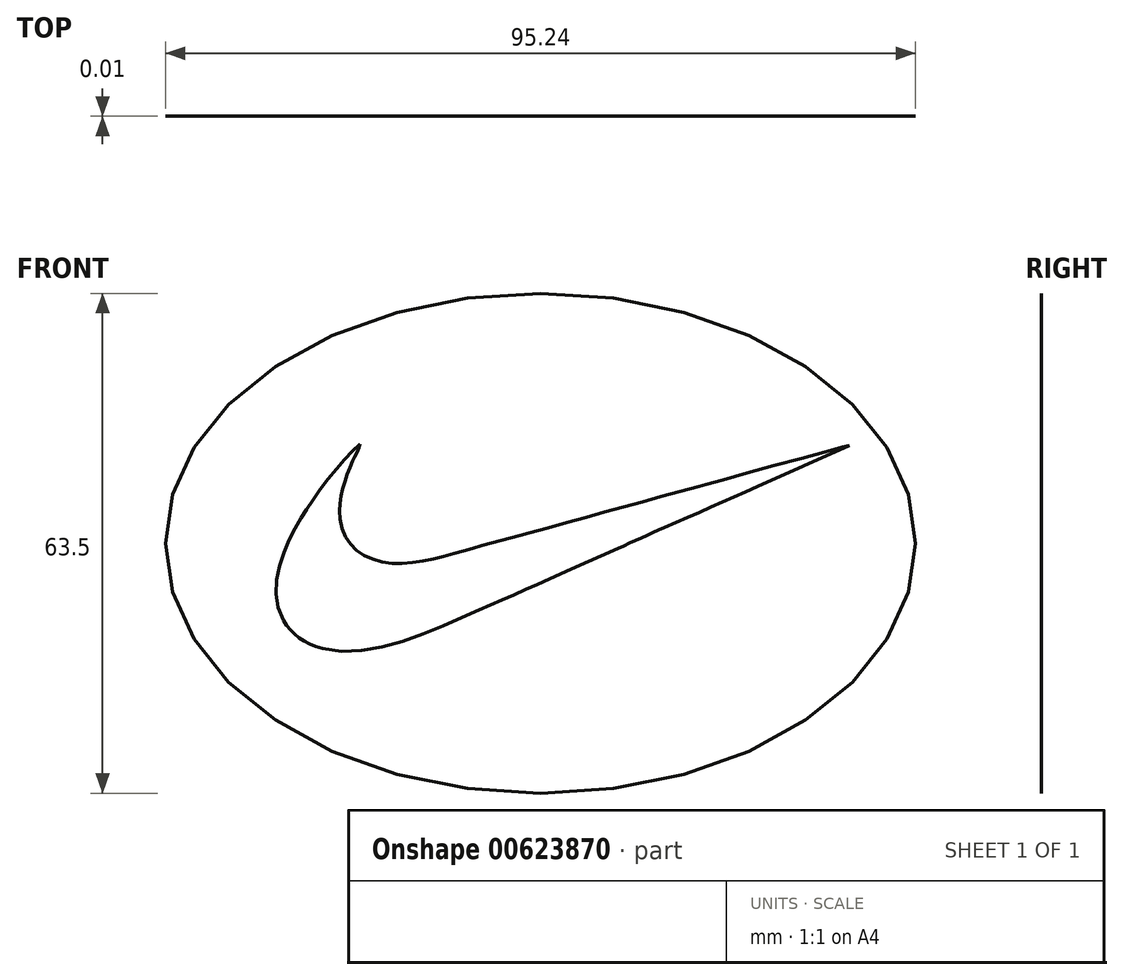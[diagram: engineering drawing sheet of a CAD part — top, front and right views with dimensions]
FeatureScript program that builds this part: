
annotation { "Feature Type Name" : "Feature", "Feature Type Description" : "" }
export const myFeature = defineFeature(function(context is Context, id is Id, definition is map)
    precondition{}
    {
        {
            var Q0;
            Q0=qCreatedBy(makeId("Front.planeOp"),FACE);
            var sketch = newSketch(context, id + "F0", { "sketchPlane" : qUnion([Q0])});
            skLineSegment(sketch, "E0", {"start": v(47.63, 0) * mm, "end": v(46.7, 6.2) * mm});
            skLineSegment(sketch, "E1", {"start": v(46.7, 6.2) * mm, "end": v(44, 12.15) * mm});
            skLineSegment(sketch, "E2", {"start": v(44, 12.15) * mm, "end": v(39.6, 17.64) * mm});
            skLineSegment(sketch, "E3", {"start": v(39.6, 17.64) * mm, "end": v(33.68, 22.45) * mm});
            skLineSegment(sketch, "E4", {"start": v(33.68, 22.45) * mm, "end": v(26.46, 26.4) * mm});
            skLineSegment(sketch, "E5", {"start": v(26.46, 26.4) * mm, "end": v(18.23, 29.33) * mm});
            skLineSegment(sketch, "E6", {"start": v(18.23, 29.33) * mm, "end": v(9.3, 31.14) * mm});
            skLineSegment(sketch, "E7", {"start": v(9.3, 31.14) * mm, "end": v(0, 31.75) * mm});
            skLineSegment(sketch, "E8", {"start": v(0, 31.75) * mm, "end": v(-9.3, 31.14) * mm});
            skLineSegment(sketch, "E9", {"start": v(-9.3, 31.14) * mm, "end": v(-18.23, 29.33) * mm});
            skLineSegment(sketch, "E10", {"start": v(-18.23, 29.33) * mm, "end": v(-26.46, 26.4) * mm});
            skLineSegment(sketch, "E11", {"start": v(-26.46, 26.4) * mm, "end": v(-33.68, 22.45) * mm});
            skLineSegment(sketch, "E12", {"start": v(-33.68, 22.45) * mm, "end": v(-39.6, 17.64) * mm});
            skLineSegment(sketch, "E13", {"start": v(-39.6, 17.64) * mm, "end": v(-44, 12.15) * mm});
            skLineSegment(sketch, "E14", {"start": v(-44, 12.15) * mm, "end": v(-46.7, 6.2) * mm});
            skLineSegment(sketch, "E15", {"start": v(-46.7, 6.2) * mm, "end": v(-47.62, 0) * mm});
            skLineSegment(sketch, "E16", {"start": v(-47.62, 0) * mm, "end": v(-46.7, -6.2) * mm});
            skLineSegment(sketch, "E17", {"start": v(-46.7, -6.2) * mm, "end": v(-44, -12.15) * mm});
            skLineSegment(sketch, "E18", {"start": v(-44, -12.15) * mm, "end": v(-39.6, -17.64) * mm});
            skLineSegment(sketch, "E19", {"start": v(-39.6, -17.64) * mm, "end": v(-33.68, -22.45) * mm});
            skLineSegment(sketch, "E20", {"start": v(-33.68, -22.45) * mm, "end": v(-26.46, -26.4) * mm});
            skLineSegment(sketch, "E21", {"start": v(-26.46, -26.4) * mm, "end": v(-18.23, -29.33) * mm});
            skLineSegment(sketch, "E22", {"start": v(-18.23, -29.33) * mm, "end": v(-9.3, -31.14) * mm});
            skLineSegment(sketch, "E23", {"start": v(-9.3, -31.14) * mm, "end": v(0, -31.75) * mm});
            skLineSegment(sketch, "E24", {"start": v(0, -31.75) * mm, "end": v(9.3, -31.14) * mm});
            skLineSegment(sketch, "E25", {"start": v(9.3, -31.14) * mm, "end": v(18.23, -29.33) * mm});
            skLineSegment(sketch, "E26", {"start": v(18.23, -29.33) * mm, "end": v(26.46, -26.4) * mm});
            skLineSegment(sketch, "E27", {"start": v(26.46, -26.4) * mm, "end": v(33.68, -22.45) * mm});
            skLineSegment(sketch, "E28", {"start": v(33.68, -22.45) * mm, "end": v(39.6, -17.64) * mm});
            skLineSegment(sketch, "E29", {"start": v(39.6, -17.64) * mm, "end": v(44, -12.15) * mm});
            skLineSegment(sketch, "E30", {"start": v(44, -12.15) * mm, "end": v(46.7, -6.2) * mm});
            skLineSegment(sketch, "E31", {"start": v(46.7, -6.2) * mm, "end": v(47.63, 0) * mm});
            skLineSegment(sketch, "E32", {"start": v(39.26, 12.43) * mm, "end": v(38.34, 12.21) * mm});
            skLineSegment(sketch, "E33", {"start": v(38.34, 12.21) * mm, "end": v(36.16, 11.63) * mm});
            skLineSegment(sketch, "E34", {"start": v(36.16, 11.63) * mm, "end": v(33.13, 10.8) * mm});
            skLineSegment(sketch, "E35", {"start": v(33.13, 10.8) * mm, "end": v(29.67, 9.86) * mm});
            skLineSegment(sketch, "E36", {"start": v(29.67, 9.86) * mm, "end": v(26.22, 8.91) * mm});
            skLineSegment(sketch, "E37", {"start": v(26.22, 8.91) * mm, "end": v(23.2, 8.08) * mm});
            skLineSegment(sketch, "E38", {"start": v(23.2, 8.08) * mm, "end": v(21.03, 7.48) * mm});
            skLineSegment(sketch, "E39", {"start": v(21.03, 7.48) * mm, "end": v(20.13, 7.23) * mm});
            skLineSegment(sketch, "E40", {"start": v(20.13, 7.23) * mm, "end": v(17.73, 6.58) * mm});
            skLineSegment(sketch, "E41", {"start": v(17.73, 6.58) * mm, "end": v(15.34, 5.93) * mm});
            skLineSegment(sketch, "E42", {"start": v(15.34, 5.93) * mm, "end": v(12.94, 5.28) * mm});
            skLineSegment(sketch, "E43", {"start": v(12.94, 5.28) * mm, "end": v(10.55, 4.63) * mm});
            skLineSegment(sketch, "E44", {"start": v(10.55, 4.63) * mm, "end": v(8.15, 3.98) * mm});
            skLineSegment(sketch, "E45", {"start": v(8.15, 3.98) * mm, "end": v(5.76, 3.32) * mm});
            skLineSegment(sketch, "E46", {"start": v(5.76, 3.32) * mm, "end": v(3.36, 2.65) * mm});
            skLineSegment(sketch, "E47", {"start": v(3.36, 2.65) * mm, "end": v(0.96, 1.98) * mm});
            skLineSegment(sketch, "E48", {"start": v(0.96, 1.98) * mm, "end": v(-0.23, 1.65) * mm});
            skLineSegment(sketch, "E49", {"start": v(-0.23, 1.65) * mm, "end": v(-1.43, 1.32) * mm});
            skLineSegment(sketch, "E50", {"start": v(-1.43, 1.32) * mm, "end": v(-2.62, 1) * mm});
            skLineSegment(sketch, "E51", {"start": v(-2.62, 1) * mm, "end": v(-3.82, 0.68) * mm});
            skLineSegment(sketch, "E52", {"start": v(-3.82, 0.68) * mm, "end": v(-5.02, 0.35) * mm});
            skLineSegment(sketch, "E53", {"start": v(-5.02, 0.35) * mm, "end": v(-6.22, 0.03) * mm});
            skLineSegment(sketch, "E54", {"start": v(-6.22, 0.03) * mm, "end": v(-7.41, -0.3) * mm});
            skLineSegment(sketch, "E55", {"start": v(-7.41, -0.3) * mm, "end": v(-8.6, -0.63) * mm});
            skLineSegment(sketch, "E56", {"start": v(-8.6, -0.63) * mm, "end": v(-9.78, -0.96) * mm});
            skLineSegment(sketch, "E57", {"start": v(-9.78, -0.96) * mm, "end": v(-11, -1.32) * mm});
            skLineSegment(sketch, "E58", {"start": v(-11, -1.32) * mm, "end": v(-12.29, -1.66) * mm});
            skLineSegment(sketch, "E59", {"start": v(-12.29, -1.66) * mm, "end": v(-13.6, -1.98) * mm});
            skLineSegment(sketch, "E60", {"start": v(-13.6, -1.98) * mm, "end": v(-14.92, -2.25) * mm});
            skLineSegment(sketch, "E61", {"start": v(-14.92, -2.25) * mm, "end": v(-16.24, -2.45) * mm});
            skLineSegment(sketch, "E62", {"start": v(-16.24, -2.45) * mm, "end": v(-17.56, -2.55) * mm});
            skLineSegment(sketch, "E63", {"start": v(-17.56, -2.55) * mm, "end": v(-18.85, -2.52) * mm});
            skLineSegment(sketch, "E64", {"start": v(-18.85, -2.52) * mm, "end": v(-20.15, -2.35) * mm});
            skLineSegment(sketch, "E65", {"start": v(-20.15, -2.35) * mm, "end": v(-21.34, -2.01) * mm});
            skLineSegment(sketch, "E66", {"start": v(-21.34, -2.01) * mm, "end": v(-22.42, -1.53) * mm});
            skLineSegment(sketch, "E67", {"start": v(-22.42, -1.53) * mm, "end": v(-23.36, -0.9) * mm});
            skLineSegment(sketch, "E68", {"start": v(-23.36, -0.9) * mm, "end": v(-24.15, -0.1) * mm});
            skLineSegment(sketch, "E69", {"start": v(-24.15, -0.1) * mm, "end": v(-24.78, 0.83) * mm});
            skLineSegment(sketch, "E70", {"start": v(-24.78, 0.83) * mm, "end": v(-25.23, 1.9) * mm});
            skLineSegment(sketch, "E71", {"start": v(-25.23, 1.9) * mm, "end": v(-25.47, 3.11) * mm});
            skLineSegment(sketch, "E72", {"start": v(-25.47, 3.11) * mm, "end": v(-25.53, 4.09) * mm});
            skLineSegment(sketch, "E73", {"start": v(-25.53, 4.09) * mm, "end": v(-25.48, 5.05) * mm});
            skLineSegment(sketch, "E74", {"start": v(-25.48, 5.05) * mm, "end": v(-25.34, 6) * mm});
            skLineSegment(sketch, "E75", {"start": v(-25.34, 6) * mm, "end": v(-25.13, 6.93) * mm});
            skLineSegment(sketch, "E76", {"start": v(-25.13, 6.93) * mm, "end": v(-24.86, 7.84) * mm});
            skLineSegment(sketch, "E77", {"start": v(-24.86, 7.84) * mm, "end": v(-24.55, 8.74) * mm});
            skLineSegment(sketch, "E78", {"start": v(-24.55, 8.74) * mm, "end": v(-24.2, 9.63) * mm});
            skLineSegment(sketch, "E79", {"start": v(-24.2, 9.63) * mm, "end": v(-23.86, 10.5) * mm});
            skLineSegment(sketch, "E80", {"start": v(-23.86, 10.5) * mm, "end": v(-23.63, 10.99) * mm});
            skLineSegment(sketch, "E81", {"start": v(-23.63, 10.99) * mm, "end": v(-23.33, 11.57) * mm});
            skLineSegment(sketch, "E82", {"start": v(-23.33, 11.57) * mm, "end": v(-23.19, 11.87) * mm});
            skLineSegment(sketch, "E83", {"start": v(-23.19, 11.87) * mm, "end": v(-23.06, 12.15) * mm});
            skLineSegment(sketch, "E84", {"start": v(-23.06, 12.15) * mm, "end": v(-22.96, 12.4) * mm});
            skLineSegment(sketch, "E85", {"start": v(-22.96, 12.4) * mm, "end": v(-22.9, 12.61) * mm});
            skLineSegment(sketch, "E86", {"start": v(-22.9, 12.61) * mm, "end": v(-23.86, 11.73) * mm});
            skLineSegment(sketch, "E87", {"start": v(-23.86, 11.73) * mm, "end": v(-24.88, 10.66) * mm});
            skLineSegment(sketch, "E88", {"start": v(-24.88, 10.66) * mm, "end": v(-25.93, 9.45) * mm});
            skLineSegment(sketch, "E89", {"start": v(-25.93, 9.45) * mm, "end": v(-26.97, 8.15) * mm});
            skLineSegment(sketch, "E90", {"start": v(-26.97, 8.15) * mm, "end": v(-27.97, 6.83) * mm});
            skLineSegment(sketch, "E91", {"start": v(-27.97, 6.83) * mm, "end": v(-28.9, 5.52) * mm});
            skLineSegment(sketch, "E92", {"start": v(-28.9, 5.52) * mm, "end": v(-29.73, 4.3) * mm});
            skLineSegment(sketch, "E93", {"start": v(-29.73, 4.3) * mm, "end": v(-30.43, 3.2) * mm});
            skLineSegment(sketch, "E94", {"start": v(-30.43, 3.2) * mm, "end": v(-31.16, 1.92) * mm});
            skLineSegment(sketch, "E95", {"start": v(-31.16, 1.92) * mm, "end": v(-31.9, 0.45) * mm});
            skLineSegment(sketch, "E96", {"start": v(-31.9, 0.45) * mm, "end": v(-32.6, -1.16) * mm});
            skLineSegment(sketch, "E97", {"start": v(-32.6, -1.16) * mm, "end": v(-33.15, -2.88) * mm});
            skLineSegment(sketch, "E98", {"start": v(-33.15, -2.88) * mm, "end": v(-33.5, -4.65) * mm});
            skLineSegment(sketch, "E99", {"start": v(-33.5, -4.65) * mm, "end": v(-33.58, -6.42) * mm});
            skLineSegment(sketch, "E100", {"start": v(-33.58, -6.42) * mm, "end": v(-33.31, -8.16) * mm});
            skLineSegment(sketch, "E101", {"start": v(-33.31, -8.16) * mm, "end": v(-32.64, -9.8) * mm});
            skLineSegment(sketch, "E102", {"start": v(-32.64, -9.8) * mm, "end": v(-32.23, -10.44) * mm});
            skLineSegment(sketch, "E103", {"start": v(-32.23, -10.44) * mm, "end": v(-31.77, -11.02) * mm});
            skLineSegment(sketch, "E104", {"start": v(-31.77, -11.02) * mm, "end": v(-31.26, -11.54) * mm});
            skLineSegment(sketch, "E105", {"start": v(-31.26, -11.54) * mm, "end": v(-30.68, -12) * mm});
            skLineSegment(sketch, "E106", {"start": v(-30.68, -12) * mm, "end": v(-30.04, -12.41) * mm});
            skLineSegment(sketch, "E107", {"start": v(-30.04, -12.41) * mm, "end": v(-29.33, -12.77) * mm});
            skLineSegment(sketch, "E108", {"start": v(-29.33, -12.77) * mm, "end": v(-28.55, -13.08) * mm});
            skLineSegment(sketch, "E109", {"start": v(-28.55, -13.08) * mm, "end": v(-27.69, -13.34) * mm});
            skLineSegment(sketch, "E110", {"start": v(-27.69, -13.34) * mm, "end": v(-25.27, -13.7) * mm});
            skLineSegment(sketch, "E111", {"start": v(-25.27, -13.7) * mm, "end": v(-22.74, -13.62) * mm});
            skLineSegment(sketch, "E112", {"start": v(-22.74, -13.62) * mm, "end": v(-20.13, -13.17) * mm});
            skLineSegment(sketch, "E113", {"start": v(-20.13, -13.17) * mm, "end": v(-17.5, -12.44) * mm});
            skLineSegment(sketch, "E114", {"start": v(-17.5, -12.44) * mm, "end": v(-14.9, -11.52) * mm});
            skLineSegment(sketch, "E115", {"start": v(-14.9, -11.52) * mm, "end": v(-12.38, -10.5) * mm});
            skLineSegment(sketch, "E116", {"start": v(-12.38, -10.5) * mm, "end": v(-10, -9.44) * mm});
            skLineSegment(sketch, "E117", {"start": v(-10, -9.44) * mm, "end": v(-7.79, -8.46) * mm});
            skLineSegment(sketch, "E118", {"start": v(-7.79, -8.46) * mm, "end": v(-6.35, -7.83) * mm});
            skLineSegment(sketch, "E119", {"start": v(-6.35, -7.83) * mm, "end": v(-4.88, -7.18) * mm});
            skLineSegment(sketch, "E120", {"start": v(-4.88, -7.18) * mm, "end": v(-3.38, -6.53) * mm});
            skLineSegment(sketch, "E121", {"start": v(-3.38, -6.53) * mm, "end": v(-1.87, -5.87) * mm});
            skLineSegment(sketch, "E122", {"start": v(-1.87, -5.87) * mm, "end": v(-0.37, -5.2) * mm});
            skLineSegment(sketch, "E123", {"start": v(-0.37, -5.2) * mm, "end": v(1.12, -4.54) * mm});
            skLineSegment(sketch, "E124", {"start": v(1.12, -4.54) * mm, "end": v(2.57, -3.89) * mm});
            skLineSegment(sketch, "E125", {"start": v(2.57, -3.89) * mm, "end": v(3.97, -3.24) * mm});
            skLineSegment(sketch, "E126", {"start": v(3.97, -3.24) * mm, "end": v(9.84, -0.63) * mm});
            skLineSegment(sketch, "E127", {"start": v(9.84, -0.63) * mm, "end": v(10.59, -0.3) * mm});
            skLineSegment(sketch, "E128", {"start": v(10.59, -0.3) * mm, "end": v(11.33, 0.03) * mm});
            skLineSegment(sketch, "E129", {"start": v(11.33, 0.03) * mm, "end": v(12.07, 0.36) * mm});
            skLineSegment(sketch, "E130", {"start": v(12.07, 0.36) * mm, "end": v(12.8, 0.7) * mm});
            skLineSegment(sketch, "E131", {"start": v(12.8, 0.7) * mm, "end": v(13.54, 1.03) * mm});
            skLineSegment(sketch, "E132", {"start": v(13.54, 1.03) * mm, "end": v(14.28, 1.36) * mm});
            skLineSegment(sketch, "E133", {"start": v(14.28, 1.36) * mm, "end": v(15.02, 1.69) * mm});
            skLineSegment(sketch, "E134", {"start": v(15.02, 1.69) * mm, "end": v(15.76, 2) * mm});
            skLineSegment(sketch, "E135", {"start": v(15.76, 2) * mm, "end": v(17.23, 2.64) * mm});
            skLineSegment(sketch, "E136", {"start": v(17.23, 2.64) * mm, "end": v(18.7, 3.28) * mm});
            skLineSegment(sketch, "E137", {"start": v(18.7, 3.28) * mm, "end": v(20.17, 3.93) * mm});
            skLineSegment(sketch, "E138", {"start": v(20.17, 3.93) * mm, "end": v(21.64, 4.6) * mm});
            skLineSegment(sketch, "E139", {"start": v(21.64, 4.6) * mm, "end": v(23.1, 5.25) * mm});
            skLineSegment(sketch, "E140", {"start": v(23.1, 5.25) * mm, "end": v(24.58, 5.9) * mm});
            skLineSegment(sketch, "E141", {"start": v(24.58, 5.9) * mm, "end": v(26.05, 6.56) * mm});
            skLineSegment(sketch, "E142", {"start": v(26.05, 6.56) * mm, "end": v(27.53, 7.2) * mm});
            skLineSegment(sketch, "E143", {"start": v(27.53, 7.2) * mm, "end": v(39.26, 12.43) * mm});
            skSolve(sketch);
        }
        {
            var Q0;
            Q0=makeQuery(id+"F0.imprint","IMPRINT",FACE,{"disambiguationData":[TD([[makeQuery(id+"F0.imprint","IMPRINT",EDGE,{"derivedFrom":sQuery(id+"F0.wireOp",EDGE,"E0")}),1.0]])]});
            extrude(context, id + "F1", {"entities" : qUnion([Q0]), "depth" : 1 / 203.2 * mm, "offsetDistance" : 25.4 * mm});
        }
        {
            var Q0;
            Q0=makeQuery(id+"F0.imprint","IMPRINT",FACE,{"disambiguationData":[TD([[makeQuery(id+"F0.imprint","IMPRINT",EDGE,{"derivedFrom":sQuery(id+"F0.wireOp",EDGE,"E32")}),1.0]])]});
            extrude(context, id + "F2", {"entities" : qUnion([Q0]), "operationType" : NewBodyOperationType.ADD, "depth" : 1 / 101.6 * mm, "offsetDistance" : 25.4 * mm});
        }
    });
